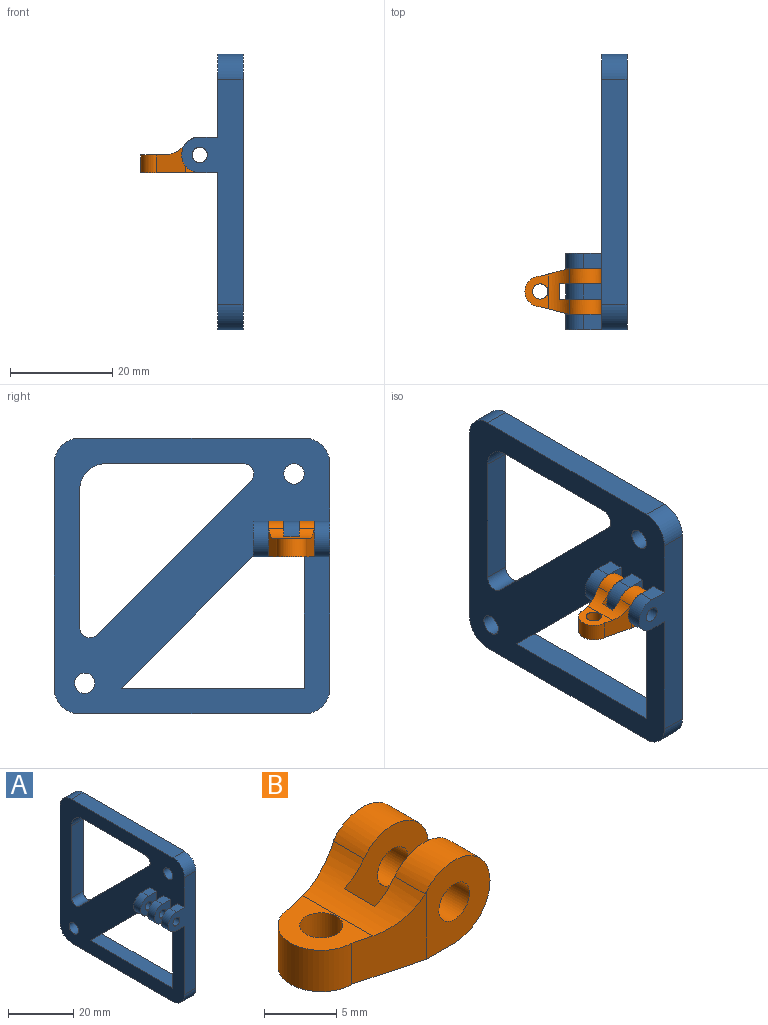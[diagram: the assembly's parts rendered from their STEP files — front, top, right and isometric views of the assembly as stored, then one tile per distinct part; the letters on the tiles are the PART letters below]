
ASSEMBLY  parts=2 mates=1
PART A: 37 faces, bbox 12x54x54 mm
  f0: plane 44x5mm, normal (0,1,0), area 220mm2, adj f1,f18,f19,f20
  f1: cylinder r=5mm len=5mm, axis (-1,0,0), area 39.3mm2, adj f0,f2,f19,f20
  f2: plane 44x5mm, normal (0,0,1), area 220mm2, adj f1,f3,f19,f20
  f3: cylinder r=5mm len=5mm, axis (-1,0,0), area 39.3mm2, adj f2,f4,f19,f20
  f4: plane 44x12mm, normal (0,-1,0), area 256.7mm2, adj f3,f5,f19,f20,f28,f30,f31,f34
  f5: cylinder r=5mm len=5mm, axis (-1,0,0), area 39.3mm2, adj f4,f6,f19,f20
  f6: plane 44x5mm, normal (0,0,-1), area 220mm2, adj f5,f18,f19,f20
  f7: plane 35.89x5mm, normal (0,0,1), area 179.5mm2, adj f8,f16,f19,f20
  f8: plane 25.76x5mm, normal (0,1,0), area 128.8mm2, adj f7,f9,f19,f20
  f9: plane 10.13x8.5mm, normal (0,0,-1), area 71.7mm2, adj f8,f16,f19,f20,f23,f24,f26,f27
  f10: cylinder r=2mm len=5mm, axis (-1,0,0), area 23.6mm2, adj f11,f17,f19,f20
  f11: plane 30.1x30.1mm, normal (0,0.71,0.71), area 212.8mm2, adj f10,f12,f19,f20
  f12: cylinder r=2mm len=5mm, axis (-1,0,0), area 23.6mm2, adj f11,f13,f19,f20
  f13: plane 27.1x5mm, normal (0,0,-1), area 135.5mm2, adj f12,f19,f20,f21
  f14: cylinder r=2mm len=5mm, axis (-1,0,0), area 62.8mm2, adj f19,f20
  f15: cylinder r=2mm len=5mm, axis (-1,0,0), area 62.8mm2, adj f19,f20
  f16: plane 25.76x25.76mm, normal (0,-0.71,-0.71), area 182.2mm2, adj f7,f9,f19,f20
  f17: plane 27.1x5mm, normal (0,-1,0), area 135.5mm2, adj f10,f19,f20,f21
  f18: cylinder r=5mm len=5mm, axis (-1,0,0), area 39.3mm2, adj f0,f6,f19,f20
  f19: plane 54x54mm, normal (1,0,0), area 1609.9mm2, adj f0,f1,f2,f3,f4,f5,f6,f7
  f20: plane 54x54mm, normal (-1,0,0), area 1546.9mm2, adj f0,f1,f2,f3,f4,f5,f6,f7
  f21: cylinder r=5mm len=5mm, axis (1,0,0), area 39.3mm2, adj f13,f17,f19,f20
  f22: plane 3.5x3mm, normal (0,0,1), area 10.5mm2, adj f20,f23,f24,f33
  f23: plane 7x7mm, normal (0,1,0), area 36.7mm2, adj f9,f20,f22,f33,f36
  f24: plane 7x7mm, normal (0,-1,0), area 36.7mm2, adj f9,f20,f22,f33,f36
  f25: plane 3.5x3mm, normal (0,0,1), area 10.5mm2, adj f20,f26,f27,f32
  f26: plane 7x7mm, normal (0,1,0), area 36.7mm2, adj f9,f20,f25,f32,f35
  f27: plane 7x7mm, normal (0,-1,0), area 36.7mm2, adj f9,f20,f25,f32,f35
  f28: plane 3.5x3mm, normal (0,0,1), area 10.5mm2, adj f4,f20,f29,f31
  f29: plane 7x7mm, normal (0,1,0), area 36.7mm2, adj f20,f28,f30,f31,f34
  f30: plane 3.5x3mm, normal (0,0,-1), area 10.5mm2, adj f4,f20,f29,f31
  f31: cylinder r=3.5mm len=7mm, axis (0,-1,0), area 33mm2, adj f4,f28,f29,f30
  f32: cylinder r=3.5mm len=7mm, axis (0,-1,0), area 33mm2, adj f9,f25,f26,f27
  f33: cylinder r=3.5mm len=7mm, axis (0,-1,0), area 33mm2, adj f9,f22,f23,f24
  f34: cylinder r=1.5mm len=3mm, axis (0,-1,0), area 28.3mm2, adj f4,f29
  f35: cylinder r=1.5mm len=3mm, axis (0,-1,0), area 28.3mm2, adj f26,f27
  f36: cylinder r=1.5mm len=3mm, axis (0,-1,0), area 28.3mm2, adj f23,f24
PART B: 16 faces, bbox 15x9x7 mm
  f0: plane 7x6.25mm, normal (0,1,0), area 30.3mm2, adj f1,f9,f10,f12
  f1: plane 5.75x5.66mm, normal (-0.25,0.97,0), area 23.5mm2, adj f0,f2,f9,f10,f14,f15
  f2: cylinder r=3mm len=6mm, axis (0,0,-1), area 33mm2, adj f1,f3,f9,f14
  f3: plane 5.75x5.66mm, normal (-0.25,-0.97,0), area 23.5mm2, adj f2,f4,f9,f11,f14,f15
  f4: plane 7x6.25mm, normal (0,-1,0), area 30.3mm2, adj f3,f9,f11,f13
  f5: plane 8.25x7mm, normal (0,1,0), area 39.7mm2, adj f8,f9,f11,f13,f15
  f6: plane 8.25x7mm, normal (0,-1,0), area 39.7mm2, adj f8,f9,f10,f12,f15
  f7: cylinder r=1.5mm len=3.5mm, axis (0,0,-1), area 33mm2, adj f9,f14
  f8: plane 3.97x3mm, normal (1,0,0), area 11.9mm2, adj f5,f6,f9,f15
  f9: plane 11.5x9mm, normal (0,0,-1), area 60.7mm2, adj f0,f1,f2,f3,f4,f5,f6,f7
  f10: cylinder r=3.5mm len=7mm, axis (0,-1,0), area 42.9mm2, adj f0,f1,f6,f9,f15
  f11: cylinder r=3.5mm len=7mm, axis (0,-1,0), area 42.9mm2, adj f3,f4,f5,f9,f15
  f12: cylinder r=1.5mm len=3mm, axis (0,-1,0), area 28.3mm2, adj f0,f6
  f13: cylinder r=1.5mm len=3mm, axis (0,-1,0), area 28.3mm2, adj f4,f5
  f14: plane 6.85x4.63mm, normal (0,0,1), area 17.5mm2, adj f1,f2,f3,f7,f15
  f15: cylinder r=5mm len=8.96mm, axis (0,-1,0), area 30.1mm2, adj f1,f3,f5,f6,f8,f10,f11,f14
PLACE A t=(-0.24,0.61,5.54)mm
PLACE B t=(-12.24,-18.89,9.31)mm
MATE fastened B.f10 <-> A.f31  axis (0,1,0) through (-3.74,-14.39,12.81)mm
